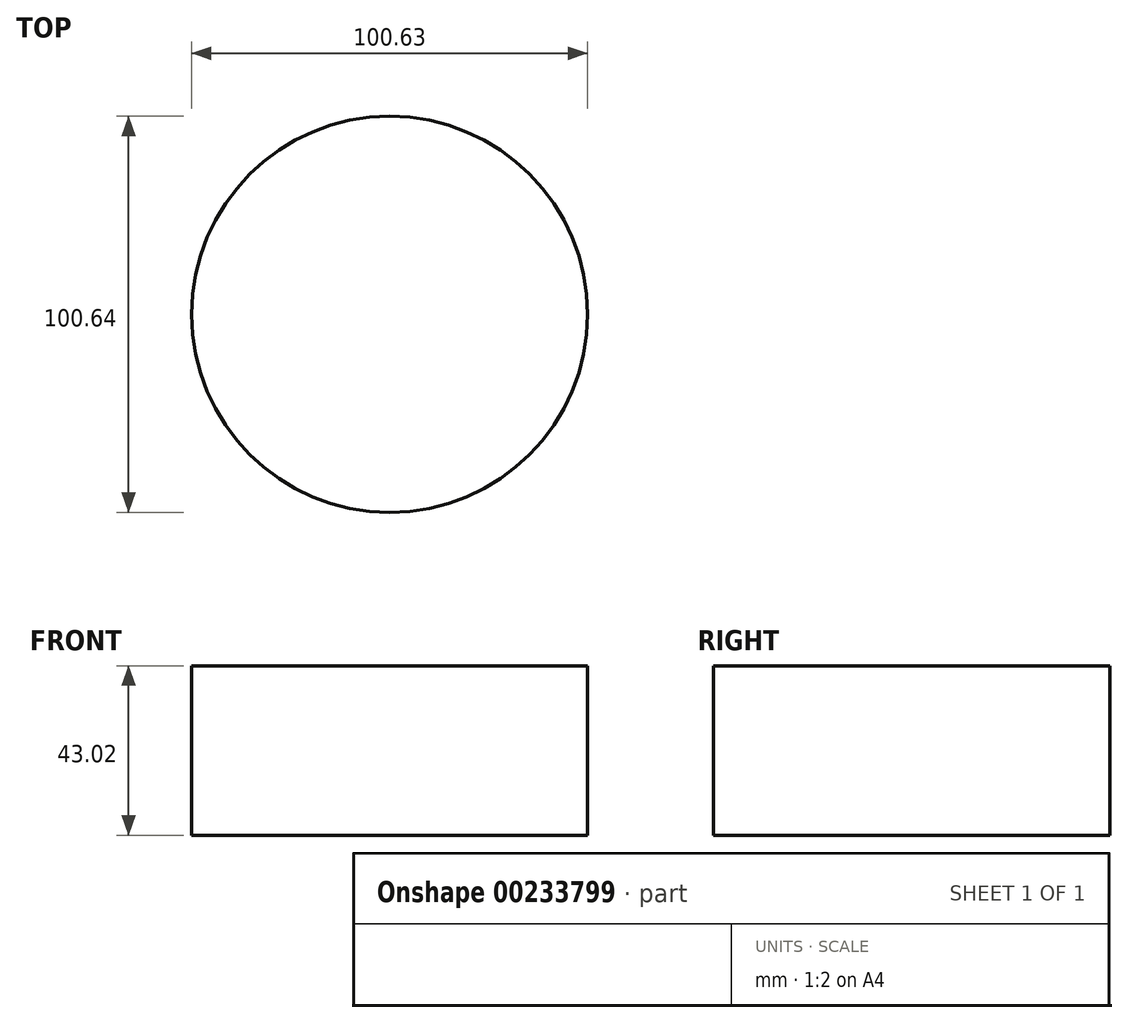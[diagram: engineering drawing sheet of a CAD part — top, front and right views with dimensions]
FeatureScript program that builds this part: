
annotation { "Feature Type Name" : "Feature", "Feature Type Description" : "" }
export const myFeature = defineFeature(function(context is Context, id is Id, definition is map)
    precondition{}
    {
        {
            var Q0;
            Q0=qCreatedBy(makeId("Top.planeOp"),FACE);
            var sketch = newSketch(context, id + "F0", { "sketchPlane" : qUnion([Q0])});
            skCircle(sketch, "E0", {"center": v(-0.41, -0.83) * mm, "radius": 50.32 * mm});
            skSolve(sketch);
        }
        {
            var Q0;
            Q0=makeQuery(id+"F0.imprint","IMPRINT",FACE,{"disambiguationData":[TD([[makeQuery(id+"F0.imprint","IMPRINT",EDGE,{"derivedFrom":sQuery(id+"F0.wireOp",EDGE,"E0")}),1.0]])]});
            extrude(context, id + "F1", {"entities" : qUnion([Q0]), "depth" : 43.02 * mm});
        }
    });
